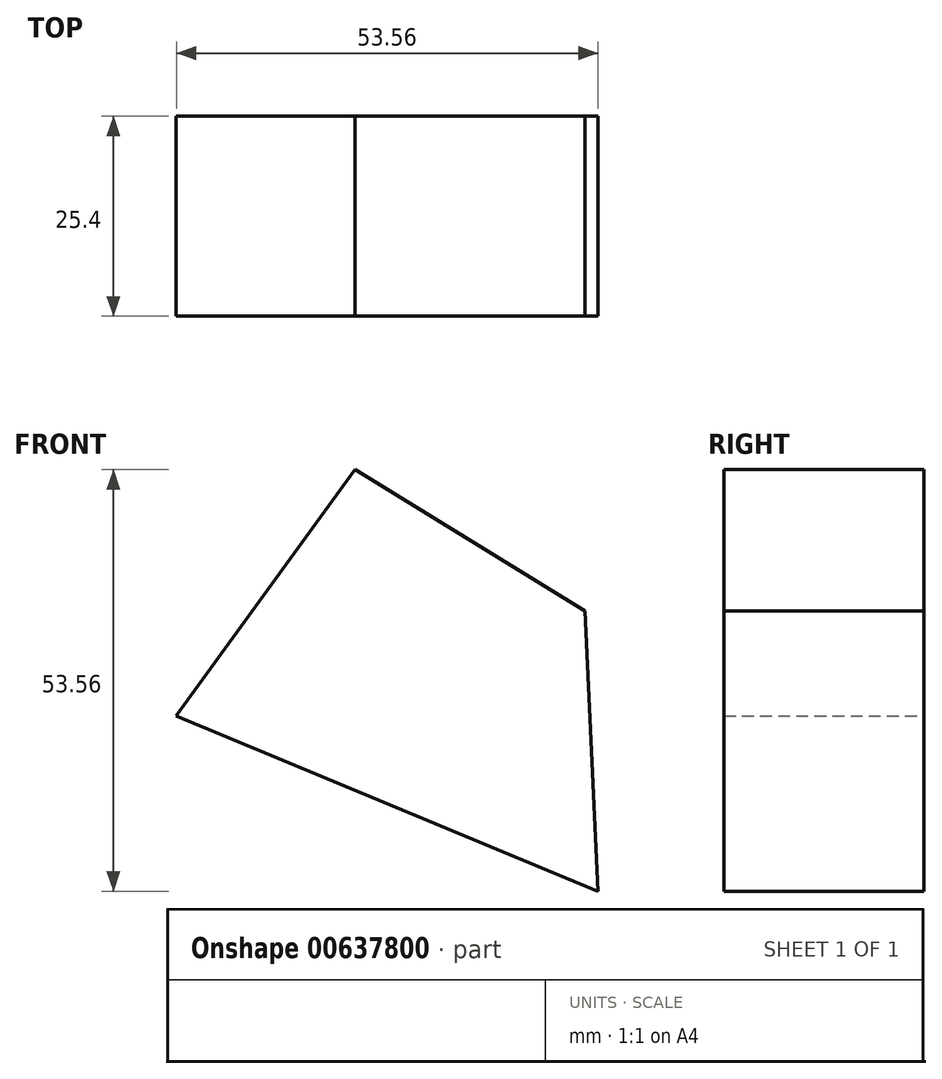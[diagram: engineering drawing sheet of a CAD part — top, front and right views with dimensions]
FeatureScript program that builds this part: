
annotation { "Feature Type Name" : "Feature", "Feature Type Description" : "" }
export const myFeature = defineFeature(function(context is Context, id is Id, definition is map)
    precondition{}
    {
        {
            var Q0;
            Q0=qCreatedBy(makeId("Front.planeOp"),FACE);
            var sketch = newSketch(context, id + "F0", { "sketchPlane" : qUnion([Q0])});
            skLineSegment(sketch, "E0", {"start": v(-30.84, 53.56) * mm, "end": v(-53.56, 22.25) * mm});
            skLineSegment(sketch, "E1", {"start": v(-53.56, 22.25) * mm, "end": v(0, 0) * mm});
            skLineSegment(sketch, "E2", {"start": v(0, 0) * mm, "end": v(-1.62, 35.61) * mm});
            skLineSegment(sketch, "E3", {"start": v(-1.62, 35.61) * mm, "end": v(-30.84, 53.56) * mm});
            skSolve(sketch);
        }
        {
            var Q0;
            Q0 = qSketchRegion(id + "F0", true);
            extrude(context, id + "F1", {"entities" : qUnion([Q0]), "depth" : 25.4 * mm, "offsetDistance" : 25.4 * mm});
        }
    });
